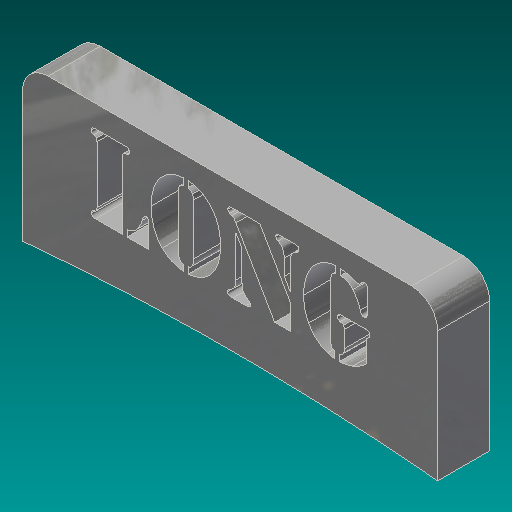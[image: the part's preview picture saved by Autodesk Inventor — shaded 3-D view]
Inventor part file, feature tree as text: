
AUTODESK INVENTOR PART (.ipt)
format: ipt  version: 2017 SP1 (Build 210196100, 196)  size: 377,856 bytes
history: native  units: in
note: dims shown in document units (in); Inventor stores cm internally (conversion verified against a paired STEP export)
features: extrude x2, sketch x2, fillet x1
ambient origin geometry x8: Origin, YZ Plane, XZ Plane, XY Plane, X Axis, Y Axis, Z Axis, Center Point
bodies: Solid1 (feature_tree)
feature tree (5):
  extrude  "Extrusion1"  Depth=1.5in
  extrude  "Extrusion2"  Depth=0.25in TaperAngle=0.0deg
  fillet  "Fillet1"  [1 undecoded]
  sketch  "Sketch1"  dims[d0=4.0in d1=1.5in]
  sketch  "Sketch2"  dims[d2=21.5in d3=0.5in d4=0.0in d5=0.0in d6=0.0in d7=0.25in]
note: 1 required parameter value undecoded (feature->parameter linkage not recoverable at this tier; creation-order binding heuristic only, values carry confidence <= 0.55)
